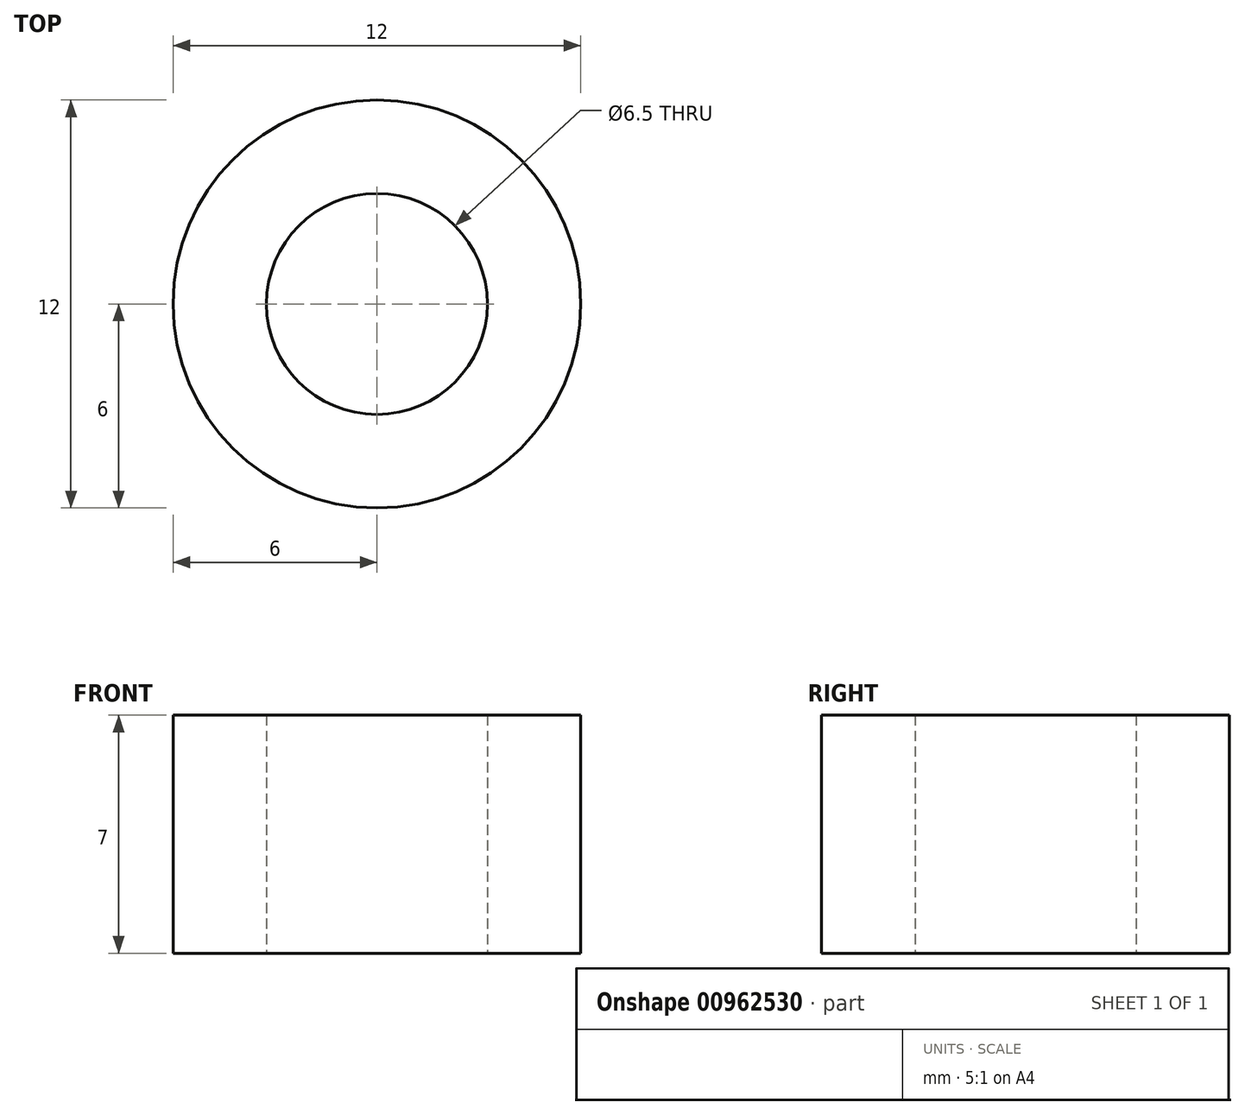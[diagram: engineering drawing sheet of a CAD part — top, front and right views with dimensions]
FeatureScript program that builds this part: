
annotation { "Feature Type Name" : "Feature", "Feature Type Description" : "" }
export const myFeature = defineFeature(function(context is Context, id is Id, definition is map)
    precondition{}
    {
        {
            var Q0;
            Q0=qCreatedBy(makeId("Top.planeOp"),FACE);
            var sketch = newSketch(context, id + "F0", { "sketchPlane" : qUnion([Q0])});
            skCircle(sketch, "E0", {"center": v(0, 0) * mm, "radius": 3.25 * mm});
            skCircle(sketch, "E1", {"center": v(0, 0) * mm, "radius": 6 * mm});
            skSolve(sketch);
        }
        {
            var Q0;
            Q0=makeQuery(id+"F0.imprint","IMPRINT",FACE,{"disambiguationData":[TD([[makeQuery(id+"F0.imprint","IMPRINT",EDGE,{"derivedFrom":sQuery(id+"F0.wireOp",EDGE,"E0")}),-1.0]])]});
            extrude(context, id + "F1", {"entities" : qUnion([Q0]), "depth" : 7 * mm, "offsetDistance" : 25.4 * mm});
        }
    });
